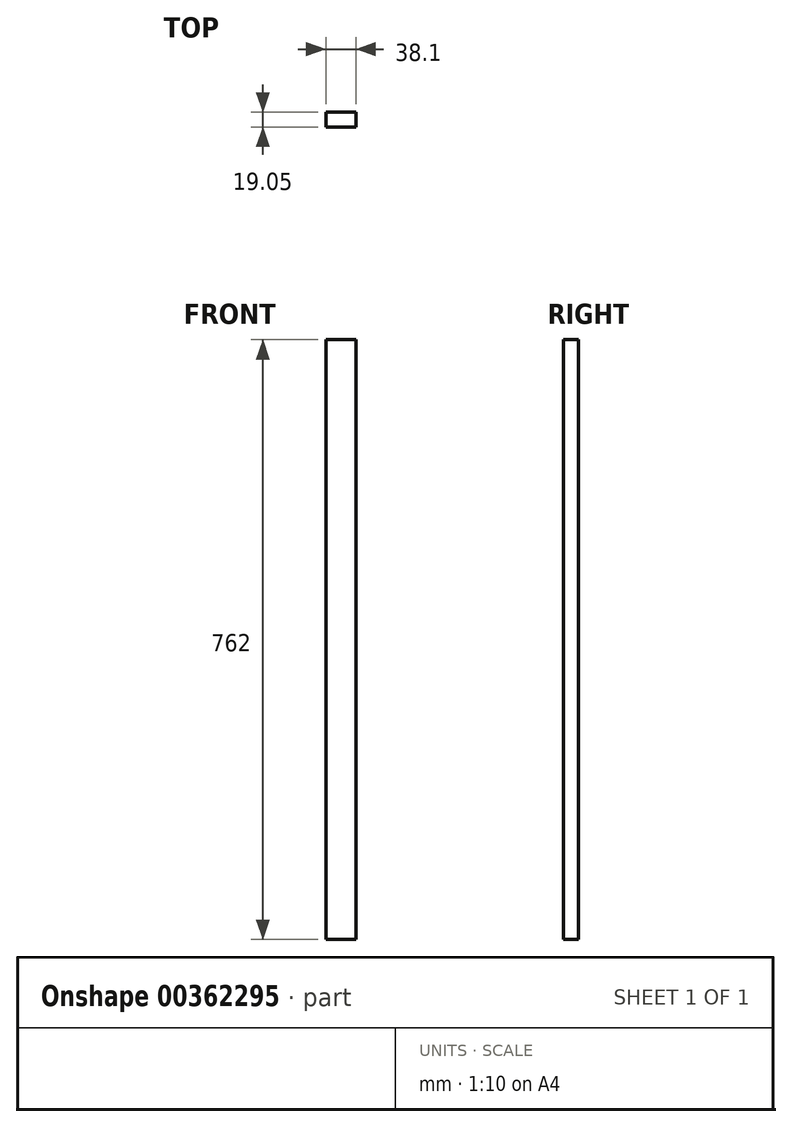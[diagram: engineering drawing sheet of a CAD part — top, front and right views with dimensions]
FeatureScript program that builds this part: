
annotation { "Feature Type Name" : "Feature", "Feature Type Description" : "" }
export const myFeature = defineFeature(function(context is Context, id is Id, definition is map)
    precondition{}
    {
        {
            var Q0;
            Q0=qCreatedBy(makeId("Front.planeOp"),FACE);
            var sketch = newSketch(context, id + "F0", { "sketchPlane" : qUnion([Q0])});
            skLineSegment(sketch, "E0.bottom", {"start": v(-54.36, 493.65) * mm, "end": v(-16.26, 493.65) * mm});
            skLineSegment(sketch, "E0.top", {"start": v(-54.36, -268.35) * mm, "end": v(-16.26, -268.35) * mm});
            skLineSegment(sketch, "E0.left", {"start": v(-54.36, 493.65) * mm, "end": v(-54.36, -268.35) * mm});
            skLineSegment(sketch, "E0.right", {"start": v(-16.26, 493.65) * mm, "end": v(-16.26, -268.35) * mm});
            skSolve(sketch);
        }
        {
            var Q0;
            Q0=makeQuery(id+"F0.imprint","IMPRINT",FACE,{"disambiguationData":[TD([[makeQuery(id+"F0.imprint","IMPRINT",EDGE,{"derivedFrom":sQuery(id+"F0.wireOp",EDGE,"E0.bottom")}),-1.0]])]});
            extrude(context, id + "F1", {"entities" : qUnion([Q0]), "depth" : 19.05 * mm});
        }
    });
